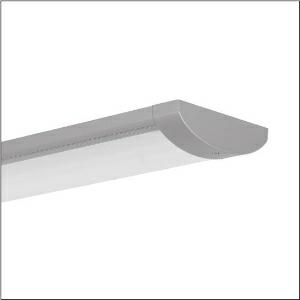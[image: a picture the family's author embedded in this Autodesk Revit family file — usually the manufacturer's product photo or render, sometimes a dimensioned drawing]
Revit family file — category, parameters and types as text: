
# Revit family: tv_20_5xa861d4n0x
name_source: partatom
category: Lighting Fixtures
units: mm (PartAtom-declared; Revit-internal decimal feet)

## family parameters
Cut with Voids When Loaded = No
Host = Face
Light Source = No
Part Type = Normal
Room Calculation Point = No
Round Connector Dimension = Use Diameter
Shared = No

## types (1)
- TV 20 (1 x LED 4000K / CRI = 80 (unbekannt), 5120 lm, 4000K)
    Apparent Load = 50 VA
    CIE Flux Codes = 48 78 95 99 100
    Color Rendering = 80
    Color Temperature = 4000K
    Default Elevation = 1800 mm
    Description = TV 20, vandal-proof luminaire, primary light control with specular reflector, of aluminium, matt, primary optical cover: enclosure, of PC, frosted, light emission: direct distribution, primary light characteristic: symmetric, installation type: surface-mounted, LED, rated luminous flux: 5.120lm, luminous efficacy: 102lm/W, light colour: 840, colour temperature: 4000K, control gear: DALI, mains connection: 230V, AC, 50Hz, rated input power: 50W, luminaire housing, of aluminium, coated, Siteco® metallic grey (DB 702S), with wall and ceiling fixing element, length: 1.561mm, width: 260mm, height: 70mm, mounting height: 2.5..4.0m, protection rating (complete): IP65, insulation class (complete): insulation class I (protective earthing), certification: CE, protection symbol: F, impact resistance: 2x IK10, standard: EN 60598, packaging unit: 1 piece
    Height = 70 mm
    Lamp = 1 x LED 4000K / CRI >= 80 (unbekannt)
    Lamp Light Flux = 5120 lm
    Lamp count = 1
    Length = 1561 mm
    Luminous efficacy = 102 lm/W
    Manufacturer = Siteco
    ModVariant = No
    Model = 5XA861D4N0X
    Mounting Place = Ceiling
    Mounting Type = Surface mounted
    Number of Poles = 1
    OnlyDefault = Yes
    Power Factor = 1
    Product Name = TV 20
    Product group = vandal-proof luminaire
    ProductGroupID = 309
    Protection Class = Protection class I
    Protection Degree = IP 65
    RLX_Detail_Level = 1
    RLX_Emergency_Light_Flux = 0 lm
    RLX_Emergency_Type = 0
    RLX_Emergency_Type_DB = No
    RlxData = <blob elided: 25289 chars, md5=2cd5d1df>
    Socket = socket
    Standby Power = 0 W
    System Light Flux = 5120 lm
    System Power = 50 W
    Type Comments = Product without accessories
    Type Image = l_1004809.jpg
    URL = http://relux.com
    VarID = ---
    Voltage = 0 V
    Weight = 0.00 kg
    Width = 260 mm

## geometry (parser evidence)
native form markers: Blend x4, Sweep x11
no freeform markers — native parametric forms only
